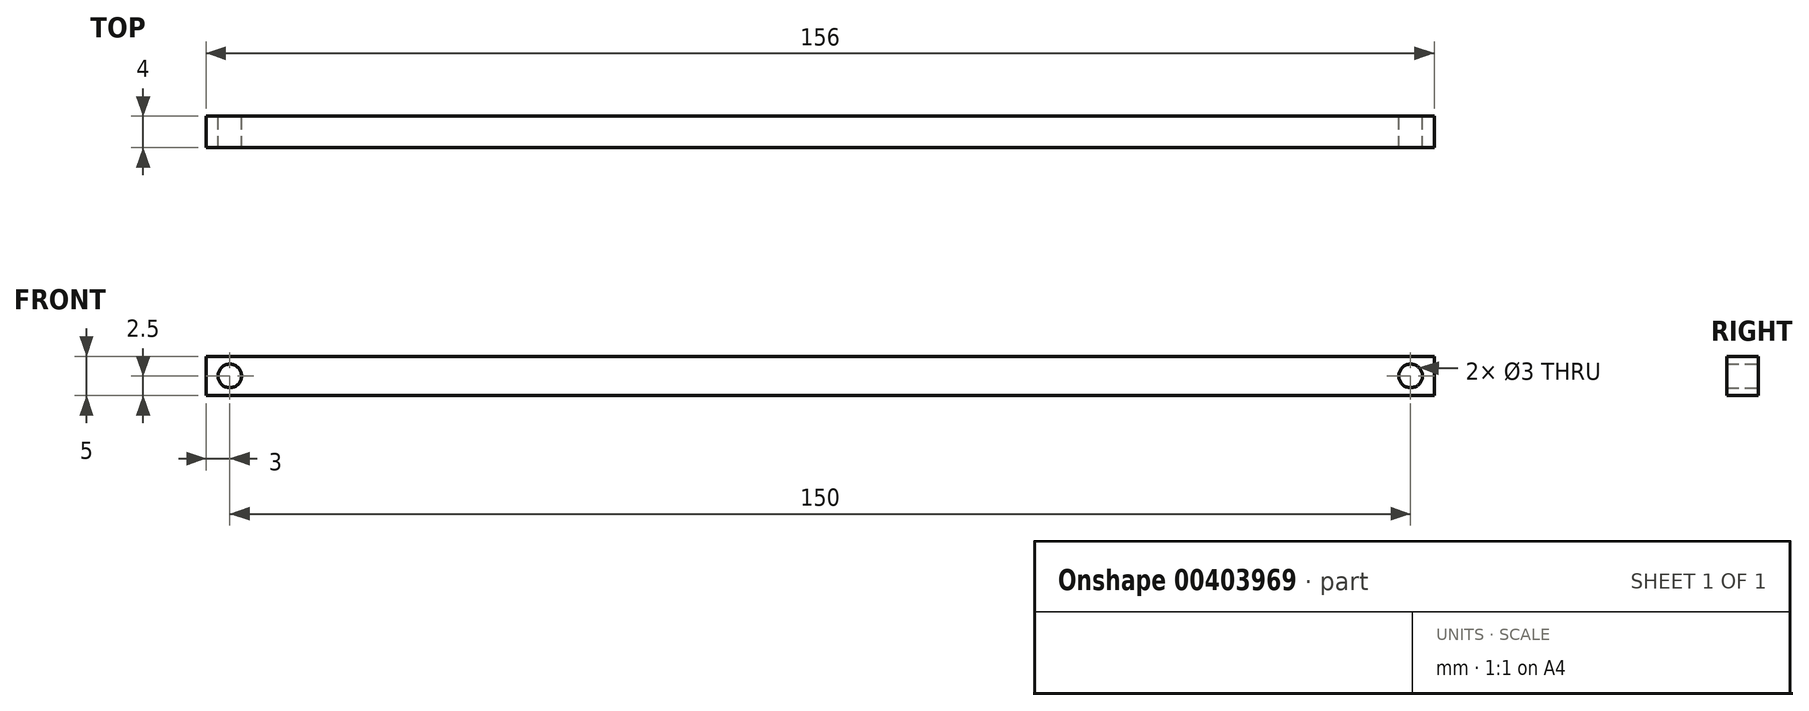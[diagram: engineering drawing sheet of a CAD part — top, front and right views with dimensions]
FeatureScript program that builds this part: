
annotation { "Feature Type Name" : "Feature", "Feature Type Description" : "" }
export const myFeature = defineFeature(function(context is Context, id is Id, definition is map)
    precondition{}
    {
        {
            var Q0;
            Q0=qCreatedBy(makeId("Front.planeOp"),FACE);
            var sketch = newSketch(context, id + "F0", { "sketchPlane" : qUnion([Q0])});
            skLineSegment(sketch, "E0.bottom", {"start": v(-103, 0) * mm, "end": v(53, 0) * mm});
            skLineSegment(sketch, "E0.top", {"start": v(-103, 5) * mm, "end": v(53, 5) * mm});
            skLineSegment(sketch, "E0.left", {"start": v(-103, 0) * mm, "end": v(-103, 5) * mm});
            skLineSegment(sketch, "E0.right", {"start": v(53, 0) * mm, "end": v(53, 5) * mm});
            skCircle(sketch, "E1", {"center": v(50, 2.5) * mm, "radius": 1.5 * mm});
            skCircle(sketch, "E2.1.0.0", {"center": v(-100, 2.5) * mm, "radius": 1.5 * mm});
            skLineSegment(sketch, "E2.direction1", {"start": v(50, 2.5) * mm, "end": v(-100, 2.5) * mm, "construction": true});
            skSolve(sketch);
        }
        {
            var Q0;
            Q0=makeQuery(id+"F0.imprint","IMPRINT",FACE,{"disambiguationData":[TD([[makeQuery(id+"F0.imprint","IMPRINT",EDGE,{"derivedFrom":sQuery(id+"F0.wireOp",EDGE,"E0.bottom")}),1.0]])]});
            var Q1;
            Q1=sQuery(id+"F0.wireOp",EDGE,"E0.top");
            extrude(context, id + "F1", {"entities" : qUnion([Q0]), "surfaceEntities" : qUnion([Q1]), "depth" : 4 * mm});
        }
    });
